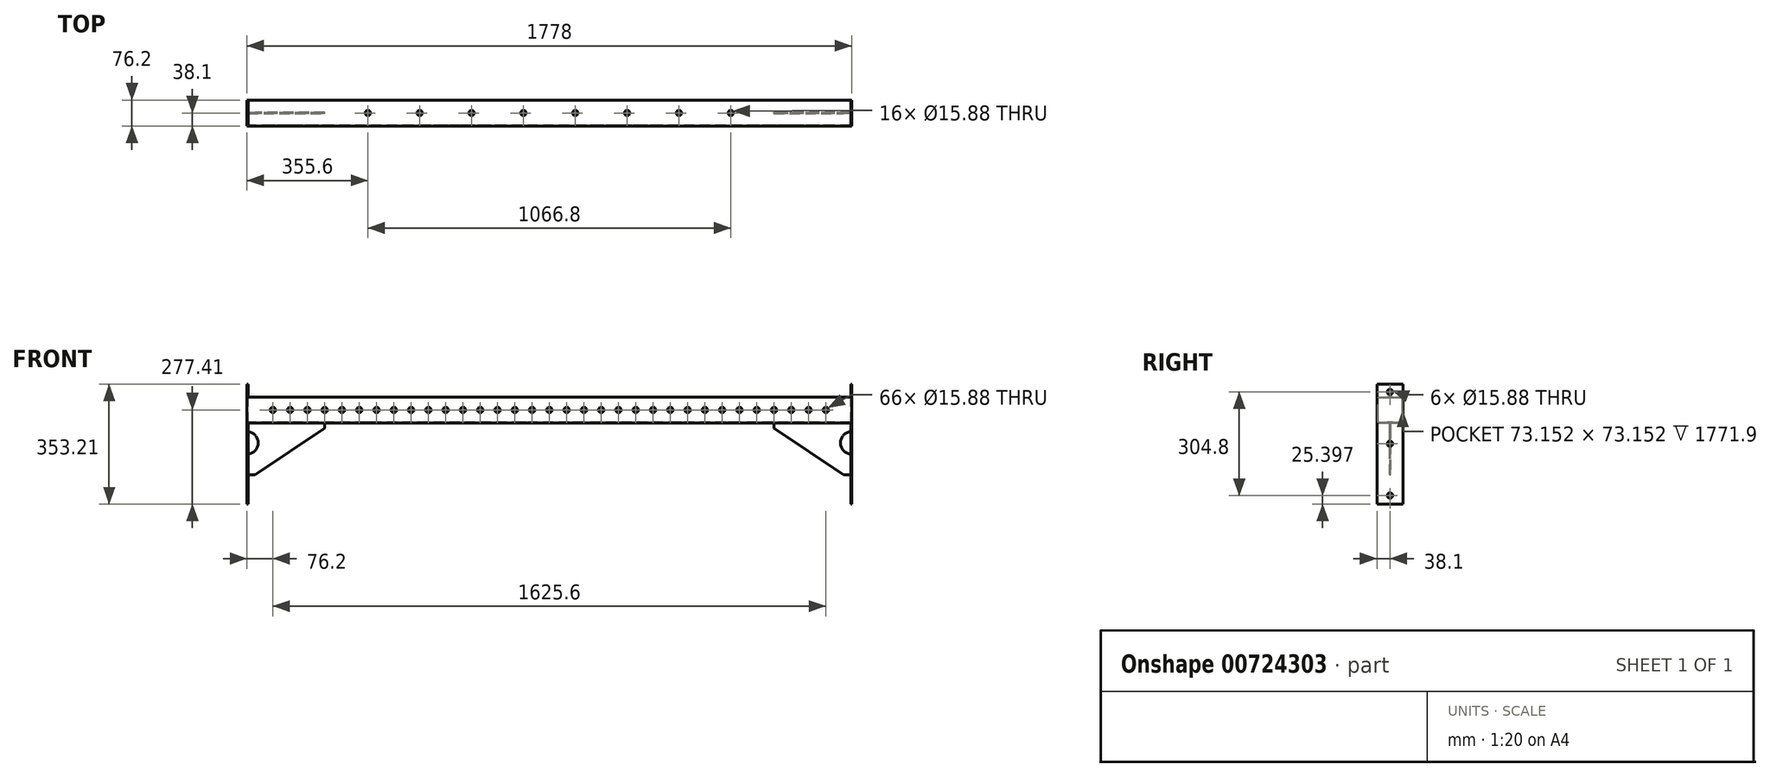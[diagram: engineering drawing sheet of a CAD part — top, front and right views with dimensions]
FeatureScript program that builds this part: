
annotation { "Feature Type Name" : "Feature", "Feature Type Description" : "" }
export const myFeature = defineFeature(function(context is Context, id is Id, definition is map)
    precondition{}
    {
        {
            var Q0;
            Q0=qCreatedBy(makeId("Right.planeOp"),FACE);
            var sketch = newSketch(context, id + "F0", { "sketchPlane" : qUnion([Q0])});
            skLineSegment(sketch, "E0.bottom", {"start": v(-38.1, -38.1) * mm, "end": v(38.1, -38.1) * mm});
            skLineSegment(sketch, "E0.top", {"start": v(-38.1, 38.1) * mm, "end": v(38.1, 38.1) * mm});
            skLineSegment(sketch, "E0.left", {"start": v(-38.1, -38.1) * mm, "end": v(-38.1, 38.1) * mm});
            skLineSegment(sketch, "E0.right", {"start": v(38.1, -38.1) * mm, "end": v(38.1, 38.1) * mm});
            skPoint(sketch, "E0.middle", {"position": v(0, 0) * mm});
            skLineSegment(sketch, "E1.bottom", {"start": v(-36.58, -36.58) * mm, "end": v(36.58, -36.58) * mm});
            skLineSegment(sketch, "E1.top", {"start": v(-36.58, 36.58) * mm, "end": v(36.58, 36.58) * mm});
            skLineSegment(sketch, "E1.left", {"start": v(-36.58, -36.58) * mm, "end": v(-36.58, 36.58) * mm});
            skLineSegment(sketch, "E1.right", {"start": v(36.58, -36.58) * mm, "end": v(36.58, 36.58) * mm});
            skSolve(sketch);
        }
        {
            var Q0;
            Q0=makeQuery(id+"F0.imprint","IMPRINT",FACE,{"disambiguationData":[TD([[makeQuery(id+"F0.imprint","IMPRINT",EDGE,{"derivedFrom":sQuery(id+"F0.wireOp",EDGE,"E0.bottom")}),1.0]])]});
            extrude(context, id + "F1", {"entities" : qUnion([Q0]), "depth" : 1778 * mm, "offsetDistance" : 25.4 * mm});
        }
        {
            var Q0;
            Q0=qCreatedBy(makeId("Front.planeOp"),FACE);
            cPlane(context, id + "F2", {"entities" : qUnion([Q0]), "cplaneType" : CPlaneType.OFFSET, "offset" : 76.2 * mm, "width" : 152.4 * mm, "height" : 152.4 * mm});
        }
        {
            var Q0;
            Q0=qCreatedBy(id+"F2.planeOp",FACE);
            var sketch = newSketch(context, id + "F3", { "sketchPlane" : qUnion([Q0])});
            skPoint(sketch, "E2", {"position": v(76.2, 0) * mm});
            skPoint(sketch, "E3.1.0.0", {"position": v(127, 0) * mm});
            skPoint(sketch, "E3.2.0.0", {"position": v(177.8, 0) * mm});
            skPoint(sketch, "E3.3.0.0", {"position": v(228.6, 0) * mm});
            skPoint(sketch, "E3.4.0.0", {"position": v(279.4, 0) * mm});
            skPoint(sketch, "E3.5.0.0", {"position": v(330.2, 0) * mm});
            skPoint(sketch, "E3.6.0.0", {"position": v(381, 0) * mm});
            skPoint(sketch, "E3.7.0.0", {"position": v(431.8, 0) * mm});
            skPoint(sketch, "E3.8.0.0", {"position": v(482.6, 0) * mm});
            skPoint(sketch, "E3.9.0.0", {"position": v(533.4, 0) * mm});
            skPoint(sketch, "E3.10.0.0", {"position": v(584.2, 0) * mm});
            skPoint(sketch, "E3.11.0.0", {"position": v(635, 0) * mm});
            skPoint(sketch, "E3.12.0.0", {"position": v(685.8, 0) * mm});
            skPoint(sketch, "E3.13.0.0", {"position": v(736.6, 0) * mm});
            skPoint(sketch, "E3.14.0.0", {"position": v(787.4, 0) * mm});
            skPoint(sketch, "E3.15.0.0", {"position": v(838.2, 0) * mm});
            skPoint(sketch, "E3.16.0.0", {"position": v(889, 0) * mm});
            skPoint(sketch, "E3.17.0.0", {"position": v(939.8, 0) * mm});
            skPoint(sketch, "E3.18.0.0", {"position": v(990.6, 0) * mm});
            skPoint(sketch, "E3.19.0.0", {"position": v(1041.4, 0) * mm});
            skPoint(sketch, "E3.20.0.0", {"position": v(1092.2, 0) * mm});
            skPoint(sketch, "E3.21.0.0", {"position": v(1143, 0) * mm});
            skPoint(sketch, "E3.22.0.0", {"position": v(1193.8, 0) * mm});
            skPoint(sketch, "E3.23.0.0", {"position": v(1244.6, 0) * mm});
            skPoint(sketch, "E3.24.0.0", {"position": v(1295.4, 0) * mm});
            skPoint(sketch, "E3.25.0.0", {"position": v(1346.2, 0) * mm});
            skPoint(sketch, "E3.26.0.0", {"position": v(1397, 0) * mm});
            skPoint(sketch, "E3.27.0.0", {"position": v(1447.8, 0) * mm});
            skPoint(sketch, "E3.28.0.0", {"position": v(1498.6, 0) * mm});
            skPoint(sketch, "E3.29.0.0", {"position": v(1549.4, 0) * mm});
            skPoint(sketch, "E3.30.0.0", {"position": v(1600.2, 0) * mm});
            skPoint(sketch, "E3.31.0.0", {"position": v(1651, 0) * mm});
            skPoint(sketch, "E3.32.0.0", {"position": v(1701.8, 0) * mm});
            skLineSegment(sketch, "E3.direction1", {"start": v(76.2, 0) * mm, "end": v(127, 0) * mm, "construction": true});
            skSolve(sketch);
        }
        {
            var Q0;
            Q0=qCreatedBy(makeId("Top.planeOp"),FACE);
            cPlane(context, id + "F4", {"entities" : qUnion([Q0]), "cplaneType" : CPlaneType.OFFSET, "offset" : 76.2 * mm, "width" : 152.4 * mm, "height" : 152.4 * mm});
        }
        {
            var Q0;
            Q0=qCreatedBy(id+"F4.planeOp",FACE);
            var sketch = newSketch(context, id + "F5", { "sketchPlane" : qUnion([Q0])});
            skPoint(sketch, "E4", {"position": v(355.6, 0) * mm});
            skPoint(sketch, "E5.1.0.0", {"position": v(508, 0) * mm});
            skPoint(sketch, "E5.2.0.0", {"position": v(660.4, 0) * mm});
            skPoint(sketch, "E5.3.0.0", {"position": v(812.8, 0) * mm});
            skPoint(sketch, "E5.4.0.0", {"position": v(965.2, 0) * mm});
            skPoint(sketch, "E5.5.0.0", {"position": v(1117.6, 0) * mm});
            skPoint(sketch, "E5.6.0.0", {"position": v(1270, 0) * mm});
            skPoint(sketch, "E5.7.0.0", {"position": v(1422.4, 0) * mm});
            skLineSegment(sketch, "E5.direction1", {"start": v(355.6, 0) * mm, "end": v(508, 0) * mm, "construction": true});
            skSolve(sketch);
        }
        {
            var Q0;
            Q0=sQuery(id+"F3.wireOp",VERTEX,"E3.direction1.start");
            var Q1;
            Q1=sQuery(id+"F3.wireOp",VERTEX,"E3.direction1.end");
            var Q2;
            Q2=sQuery(id+"F3.wireOp",VERTEX,"E3.2.0.0");
            var Q3;
            Q3=sQuery(id+"F3.wireOp",VERTEX,"E3.3.0.0");
            var Q4;
            Q4=sQuery(id+"F3.wireOp",VERTEX,"E3.4.0.0");
            var Q5;
            Q5=sQuery(id+"F3.wireOp",VERTEX,"E3.5.0.0");
            var Q6;
            Q6=sQuery(id+"F3.wireOp",VERTEX,"E3.6.0.0");
            var Q7;
            Q7=sQuery(id+"F3.wireOp",VERTEX,"E3.7.0.0");
            var Q8;
            Q8=sQuery(id+"F3.wireOp",VERTEX,"E3.8.0.0");
            var Q9;
            Q9=sQuery(id+"F3.wireOp",VERTEX,"E3.9.0.0");
            var Q10;
            Q10=sQuery(id+"F3.wireOp",VERTEX,"E3.10.0.0");
            var Q11;
            Q11=sQuery(id+"F3.wireOp",VERTEX,"E3.11.0.0");
            var Q12;
            Q12=sQuery(id+"F3.wireOp",VERTEX,"E3.12.0.0");
            var Q13;
            Q13=sQuery(id+"F3.wireOp",VERTEX,"E3.13.0.0");
            var Q14;
            Q14=sQuery(id+"F3.wireOp",VERTEX,"E3.14.0.0");
            var Q15;
            Q15=sQuery(id+"F3.wireOp",VERTEX,"E3.15.0.0");
            var Q16;
            Q16=sQuery(id+"F3.wireOp",VERTEX,"E3.16.0.0");
            var Q17;
            Q17=sQuery(id+"F3.wireOp",VERTEX,"E3.17.0.0");
            var Q18;
            Q18=sQuery(id+"F3.wireOp",VERTEX,"E3.18.0.0");
            var Q19;
            Q19=sQuery(id+"F3.wireOp",VERTEX,"E3.19.0.0");
            var Q20;
            Q20=sQuery(id+"F3.wireOp",VERTEX,"E3.20.0.0");
            var Q21;
            Q21=sQuery(id+"F3.wireOp",VERTEX,"E3.21.0.0");
            var Q22;
            Q22=sQuery(id+"F3.wireOp",VERTEX,"E3.22.0.0");
            var Q23;
            Q23=sQuery(id+"F3.wireOp",VERTEX,"E3.23.0.0");
            var Q24;
            Q24=sQuery(id+"F3.wireOp",VERTEX,"E3.24.0.0");
            var Q25;
            Q25=sQuery(id+"F3.wireOp",VERTEX,"E3.25.0.0");
            var Q26;
            Q26=sQuery(id+"F3.wireOp",VERTEX,"E3.26.0.0");
            var Q27;
            Q27=sQuery(id+"F3.wireOp",VERTEX,"E3.27.0.0");
            var Q28;
            Q28=sQuery(id+"F3.wireOp",VERTEX,"E3.28.0.0");
            var Q29;
            Q29=sQuery(id+"F3.wireOp",VERTEX,"E3.29.0.0");
            var Q30;
            Q30=sQuery(id+"F3.wireOp",VERTEX,"E3.30.0.0");
            var Q31;
            Q31=sQuery(id+"F3.wireOp",VERTEX,"E3.31.0.0");
            var Q32;
            Q32=sQuery(id+"F3.wireOp",VERTEX,"E3.32.0.0");
            var Q33;
            Q33=sQuery(id+"F5.wireOp",VERTEX,"E5.7.0.0");
            var Q34;
            Q34=sQuery(id+"F5.wireOp",VERTEX,"E5.6.0.0");
            var Q35;
            Q35=sQuery(id+"F5.wireOp",VERTEX,"E5.5.0.0");
            var Q36;
            Q36=sQuery(id+"F5.wireOp",VERTEX,"E5.4.0.0");
            var Q37;
            Q37=sQuery(id+"F5.wireOp",VERTEX,"E5.3.0.0");
            var Q38;
            Q38=sQuery(id+"F5.wireOp",VERTEX,"E5.2.0.0");
            var Q39;
            Q39=sQuery(id+"F5.wireOp",VERTEX,"E5.1.0.0");
            var Q40;
            Q40=sQuery(id+"F5.wireOp",VERTEX,"E4");
            var Q41;
            Q41=makeQuery(id+"F1.opExtrude","SWEPT_BODY",BODY,{"disambiguationData":[OSD([sQuery(id+"F0.wireOp",EDGE,"E0.bottom"),sQuery(id+"F0.wireOp",EDGE,"E0.top"),sQuery(id+"F0.wireOp",EDGE,"E0.left"),sQuery(id+"F0.wireOp",EDGE,"E0.right"),sQuery(id+"F0.wireOp",EDGE,"E1.bottom"),sQuery(id+"F0.wireOp",EDGE,"E1.top"),sQuery(id+"F0.wireOp",EDGE,"E1.left"),sQuery(id+"F0.wireOp",EDGE,"E1.right")])]});
            hole(context, id + "F6", {"style" : HoleStyle.SIMPLE, "endStyle" : HoleEndStyle.THROUGH, "holeDiameter" : 15.88 * mm, "majorDiameter" : 6.35 * mm, "isTappedThrough" : true, "tappedDepth" : 12.7 * mm, "tapClearance" : 3, "locations" : qUnion([Q0, Q1, Q2, Q3, Q4, Q5, Q6, Q7, Q8, Q9, Q10, Q11, Q12, Q13, Q14, Q15, Q16, Q17, Q18, Q19, Q20, Q21, Q22, Q23, Q24, Q25, Q26, Q27, Q28, Q29, Q30, Q31, Q32, Q33, Q34, Q35, Q36, Q37, Q38, Q39, Q40]), "scope" : qUnion([Q41])});
        }
        {
            var Q0;
            Q0=qCreatedBy(makeId("Front.planeOp"),FACE);
            var sketch = newSketch(context, id + "F7", { "sketchPlane" : qUnion([Q0])});
            skLineSegment(sketch, "E6.bottom", {"start": v(0, -38.1) * mm, "end": v(228.6, -38.1) * mm});
            skLineSegment(sketch, "E6.left", {"start": v(0, -38.1) * mm, "end": v(0, -190.5) * mm});
            skLineSegment(sketch, "E7", {"start": v(228.6, -54.18) * mm, "end": v(24, -190.5) * mm});
            skLineSegment(sketch, "E8", {"start": v(0, -190.5) * mm, "end": v(24, -190.5) * mm});
            skLineSegment(sketch, "E9", {"start": v(228.6, -38.1) * mm, "end": v(228.6, -54.18) * mm});
            skArc(sketch, "E10", {"start": v(0, -130.38) * mm, "mid": v(33.2, -97.17) * mm, "end": v(0, -63.96) * mm});
            skSolve(sketch);
        }
        {
            var Q0;
            {var subQ3=sQuery(id+"F7.wireOp",EDGE,"E6.bottom");Q0=makeQuery(id+"F7.imprint","IMPRINT",FACE,{"disambiguationData":[TD([[makeQuery(id+"F7.imprint","IMPRINT",EDGE,{"derivedFrom":subQ3}),-1.0]])]});}
            extrude(context, id + "F8", {"entities" : qUnion([Q0]), "operationType" : NewBodyOperationType.ADD, "depth" : 1.52 * mm, "offsetDistance" : 25.4 * mm});
        }
        {
            var Q0;
            {var subQ3=sQuery(id+"F7.wireOp",EDGE,"E6.bottom");Q0=makeQuery(id+"F7.imprint","IMPRINT",FACE,{"disambiguationData":[TD([[makeQuery(id+"F7.imprint","IMPRINT",EDGE,{"derivedFrom":subQ3}),-1.0]])]});}
            extrude(context, id + "F9", {"entities" : qUnion([Q0]), "operationType" : NewBodyOperationType.ADD, "oppositeDirection" : true, "depth" : 1.52 * mm, "offsetDistance" : 25.4 * mm});
        }
        {
            var Q0;
            Q0=qCreatedBy(makeId("Right.planeOp"),FACE);
            var sketch = newSketch(context, id + "F10", { "sketchPlane" : qUnion([Q0])});
            skLineSegment(sketch, "E11.bottom", {"start": v(38.1, 75.8) * mm, "end": v(-38.1, 75.8) * mm});
            skLineSegment(sketch, "E11.top", {"start": v(38.1, -277.41) * mm, "end": v(-38.1, -277.41) * mm});
            skLineSegment(sketch, "E11.left", {"start": v(38.1, 75.8) * mm, "end": v(38.1, -277.41) * mm});
            skLineSegment(sketch, "E11.right", {"start": v(-38.1, 75.8) * mm, "end": v(-38.1, -277.41) * mm});
            skCircle(sketch, "E12", {"center": v(0, -252.01) * mm, "radius": 7.94 * mm});
            skCircle(sketch, "E13", {"center": v(0, -99.61) * mm, "radius": 7.94 * mm});
            skCircle(sketch, "E14", {"center": v(0, 52.79) * mm, "radius": 7.94 * mm});
            skSolve(sketch);
        }
        {
            var Q0;
            Q0=makeQuery(id+"F10.imprint","IMPRINT",FACE,{"disambiguationData":[TD([[makeQuery(id+"F10.imprint","IMPRINT",EDGE,{"derivedFrom":sQuery(id+"F10.wireOp",EDGE,"E11.bottom")}),1.0]])]});
            extrude(context, id + "F11", {"entities" : qUnion([Q0]), "operationType" : NewBodyOperationType.ADD, "depth" : 3.05 * mm, "offsetDistance" : 25.4 * mm});
        }
        {
            var Q0;
            Q0=qCreatedBy(makeId("Right.planeOp"),FACE);
            cPlane(context, id + "F12", {"entities" : qUnion([Q0]), "cplaneType" : CPlaneType.OFFSET, "offset" : 889 * mm, "width" : 152.4 * mm, "height" : 152.4 * mm});
        }
        {
            var Q0;
            Q0=makeQuery(id+"F1.opExtrude","SWEPT_BODY",BODY,{"disambiguationData":[OSD([sQuery(id+"F0.wireOp",EDGE,"E0.bottom"),sQuery(id+"F0.wireOp",EDGE,"E0.top"),sQuery(id+"F0.wireOp",EDGE,"E0.left"),sQuery(id+"F0.wireOp",EDGE,"E0.right"),sQuery(id+"F0.wireOp",EDGE,"E1.bottom"),sQuery(id+"F0.wireOp",EDGE,"E1.top"),sQuery(id+"F0.wireOp",EDGE,"E1.left"),sQuery(id+"F0.wireOp",EDGE,"E1.right")])]});
            var Q1;
            Q1=qCreatedBy(id+"F12.planeOp",FACE);
            mirror(context, id + "F13", {"operationType" : NewBodyOperationType.ADD, "entities" : qUnion([Q0]), "mirrorPlane" : qUnion([Q1])});
        }
    });
